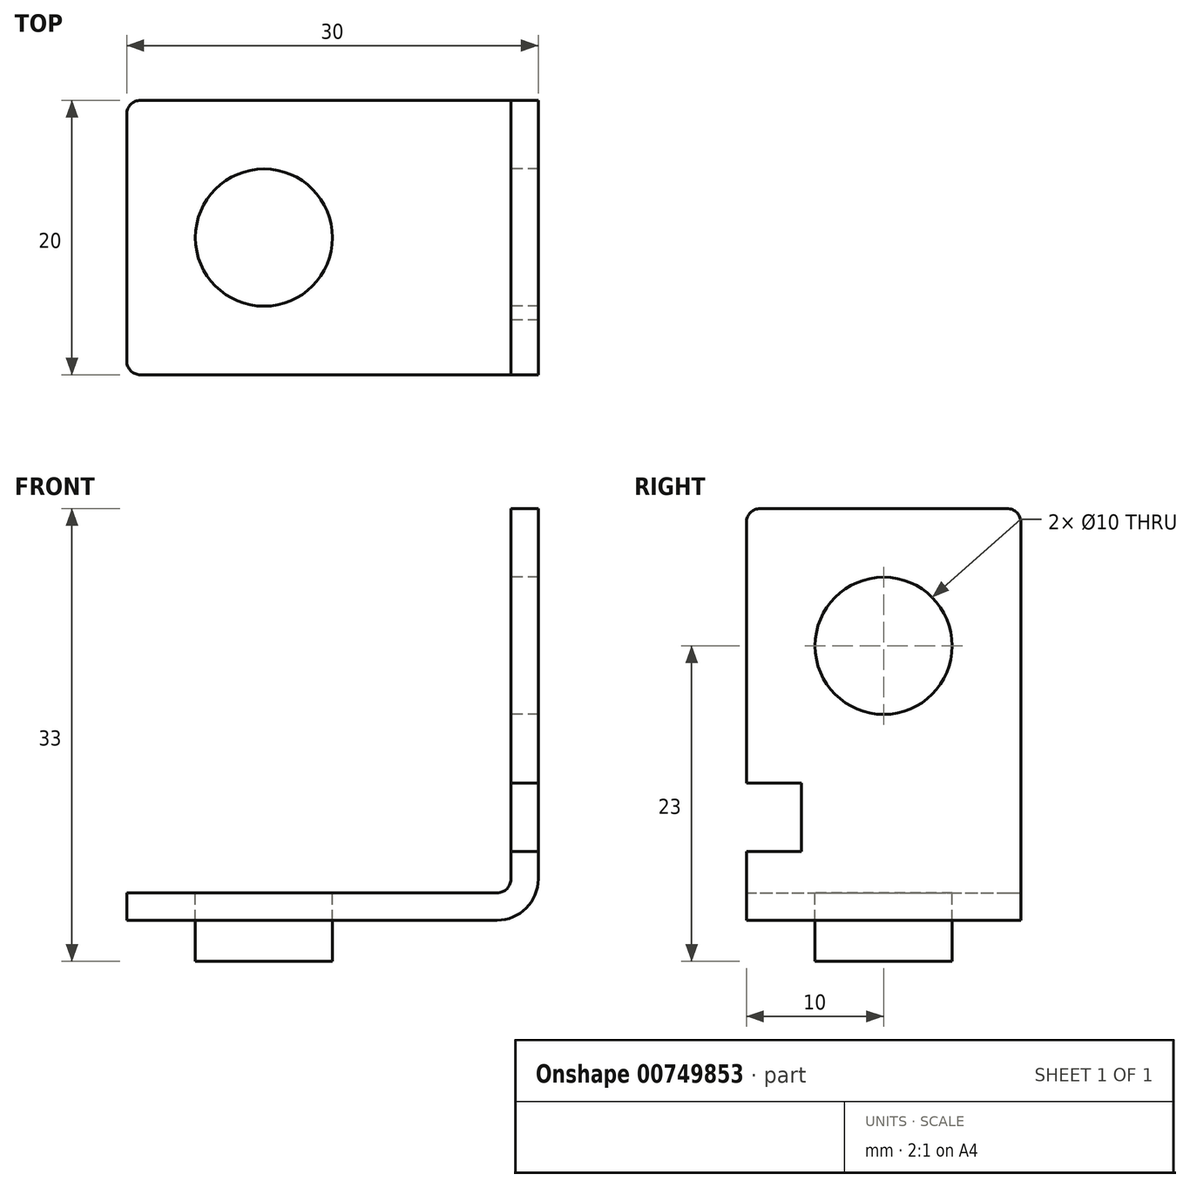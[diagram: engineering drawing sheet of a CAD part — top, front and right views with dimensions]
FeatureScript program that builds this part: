
annotation { "Feature Type Name" : "Feature", "Feature Type Description" : "" }
export const myFeature = defineFeature(function(context is Context, id is Id, definition is map)
    precondition{}
    {
        {
            var Q0;
            Q0=qCreatedBy(makeId("Front.planeOp"),FACE);
            var sketch = newSketch(context, id + "F0", { "sketchPlane" : qUnion([Q0])});
            skLineSegment(sketch, "E0", {"start": v(0, 3) * mm, "end": v(0, 30) * mm});
            skLineSegment(sketch, "E1", {"start": v(-3, 0) * mm, "end": v(-30, 0) * mm});
            skPoint(sketch, "E2.visualSharp", {"position": v(0, 0) * mm});
            skArc(sketch, "E2.filletArc", {"start": v(-3, 0) * mm, "mid": v(-0.88, 0.88) * mm, "end": v(0, 3) * mm});
            skLineSegment(sketch, "E3.0", {"start": v(-2, 3) * mm, "end": v(-2, 30) * mm});
            skLineSegment(sketch, "E3.1", {"start": v(-3, 2) * mm, "end": v(-30, 2) * mm});
            skPoint(sketch, "E4.visualSharp", {"position": v(-2, 2) * mm});
            skArc(sketch, "E4.filletArc", {"start": v(-3, 2) * mm, "mid": v(-2.3, 2.3) * mm, "end": v(-2, 3) * mm});
            skLineSegment(sketch, "E5", {"start": v(-30, 2) * mm, "end": v(-30, 0) * mm});
            skLineSegment(sketch, "E6", {"start": v(-2, 30) * mm, "end": v(0, 30) * mm});
            skSolve(sketch);
        }
        {
            var Q0;
            Q0 = qSketchRegion(id + "F0", true);
            extrude(context, id + "F1", {"entities" : qUnion([Q0]), "depth" : 20 * mm, "offsetDistance" : 25 * mm});
        }
        {
            var Q0;
            Q0=makeQuery(id+"F1.opExtrude","SWEPT_FACE",FACE,{"disambiguationData":[OSD([sQuery(id+"F0.wireOp",EDGE,"E3.1")])]});
            var sketch = newSketch(context, id + "F2", { "sketchPlane" : qUnion([Q0])});
            skCircle(sketch, "E7", {"center": v(-20, -10) * mm, "radius": 5 * mm});
            skSolve(sketch);
        }
        {
            var Q0;
            Q0 = qSketchRegion(id + "F2", true);
            extrude(context, id + "F3", {"entities" : qUnion([Q0]), "operationType" : NewBodyOperationType.REMOVE, "endBound" : BoundingType.UP_TO_NEXT, "oppositeDirection" : true, "depth" : 25 * mm, "offsetDistance" : 25 * mm});
        }
        {
            var Q0;
            Q0=makeQuery(id+"F1.opExtrude","SWEPT_FACE",FACE,{"disambiguationData":[OSD([sQuery(id+"F0.wireOp",EDGE,"E3.0")])]});
            var sketch = newSketch(context, id + "F4", { "sketchPlane" : qUnion([Q0])});
            skCircle(sketch, "E8", {"center": v(10, 20) * mm, "radius": 5 * mm});
            skSolve(sketch);
        }
        {
            var Q0;
            Q0 = qSketchRegion(id + "F4", true);
            extrude(context, id + "F5", {"entities" : qUnion([Q0]), "operationType" : NewBodyOperationType.REMOVE, "endBound" : BoundingType.UP_TO_NEXT, "oppositeDirection" : true, "depth" : 25 * mm, "offsetDistance" : 25 * mm});
        }
        {
            var Q0;
            Q0=makeQuery(id+"F1.opExtrude","SWEPT_FACE",FACE,{"disambiguationData":[OSD([sQuery(id+"F0.wireOp",EDGE,"E3.0")])]});
            var sketch = newSketch(context, id + "F6", { "sketchPlane" : qUnion([Q0])});
            skLineSegment(sketch, "E9", {"start": v(20, 10) * mm, "end": v(16, 10) * mm});
            skLineSegment(sketch, "E10", {"start": v(16, 10) * mm, "end": v(16, 5) * mm});
            skLineSegment(sketch, "E11", {"start": v(16, 5) * mm, "end": v(20, 5) * mm});
            skLineSegment(sketch, "E12", {"start": v(20, 5) * mm, "end": v(20, 10) * mm});
            skSolve(sketch);
        }
        {
            var Q0;
            Q0 = qSketchRegion(id + "F6", true);
            extrude(context, id + "F7", {"entities" : qUnion([Q0]), "operationType" : NewBodyOperationType.REMOVE, "endBound" : BoundingType.UP_TO_NEXT, "oppositeDirection" : true, "depth" : 25 * mm, "offsetDistance" : 25 * mm});
        }
        {
            var Q0;
            Q0=makeQuery(id+"F1.opExtrude","CAP_EDGE",EDGE,{"disambiguationData":[OSD([sQuery(id+"F0.wireOp",EDGE,"E6")])],"isStart":false});
            var Q1;
            Q1=makeQuery(id+"F1.opExtrude","CAP_EDGE",EDGE,{"disambiguationData":[OSD([sQuery(id+"F0.wireOp",EDGE,"E6")])],"isStart":true});
            var Q2;
            Q2=makeQuery(id+"F1.opExtrude","CAP_EDGE",EDGE,{"disambiguationData":[OSD([sQuery(id+"F0.wireOp",EDGE,"E5")])],"isStart":false});
            var Q3;
            Q3=makeQuery(id+"F1.opExtrude","CAP_EDGE",EDGE,{"disambiguationData":[OSD([sQuery(id+"F0.wireOp",EDGE,"E5")])],"isStart":true});
            fillet(context, id + "F8", {"entities" : qUnion([Q0, Q1, Q2, Q3]), "radius" : 1 * mm, "tangentPropagation" : true, "allowEdgeOverflow" : false});
        }
        {
            var Q0;
            Q0=makeQuery(id+"F1.opExtrude","SWEPT_FACE",FACE,{"disambiguationData":[OSD([sQuery(id+"F0.wireOp",EDGE,"E3.1")])]});
            var sketch = newSketch(context, id + "F9", { "sketchPlane" : qUnion([Q0])});
            skCircle(sketch, "E13.0", {"center": v(-20, -10) * mm, "radius": 5 * mm});
            skSolve(sketch);
        }
        {
            var Q0;
            Q0 = qSketchRegion(id + "F9", true);
            extrude(context, id + "F10", {"entities" : qUnion([Q0]), "oppositeDirection" : true, "depth" : 5 * mm, "offsetDistance" : 25 * mm});
        }
    });
